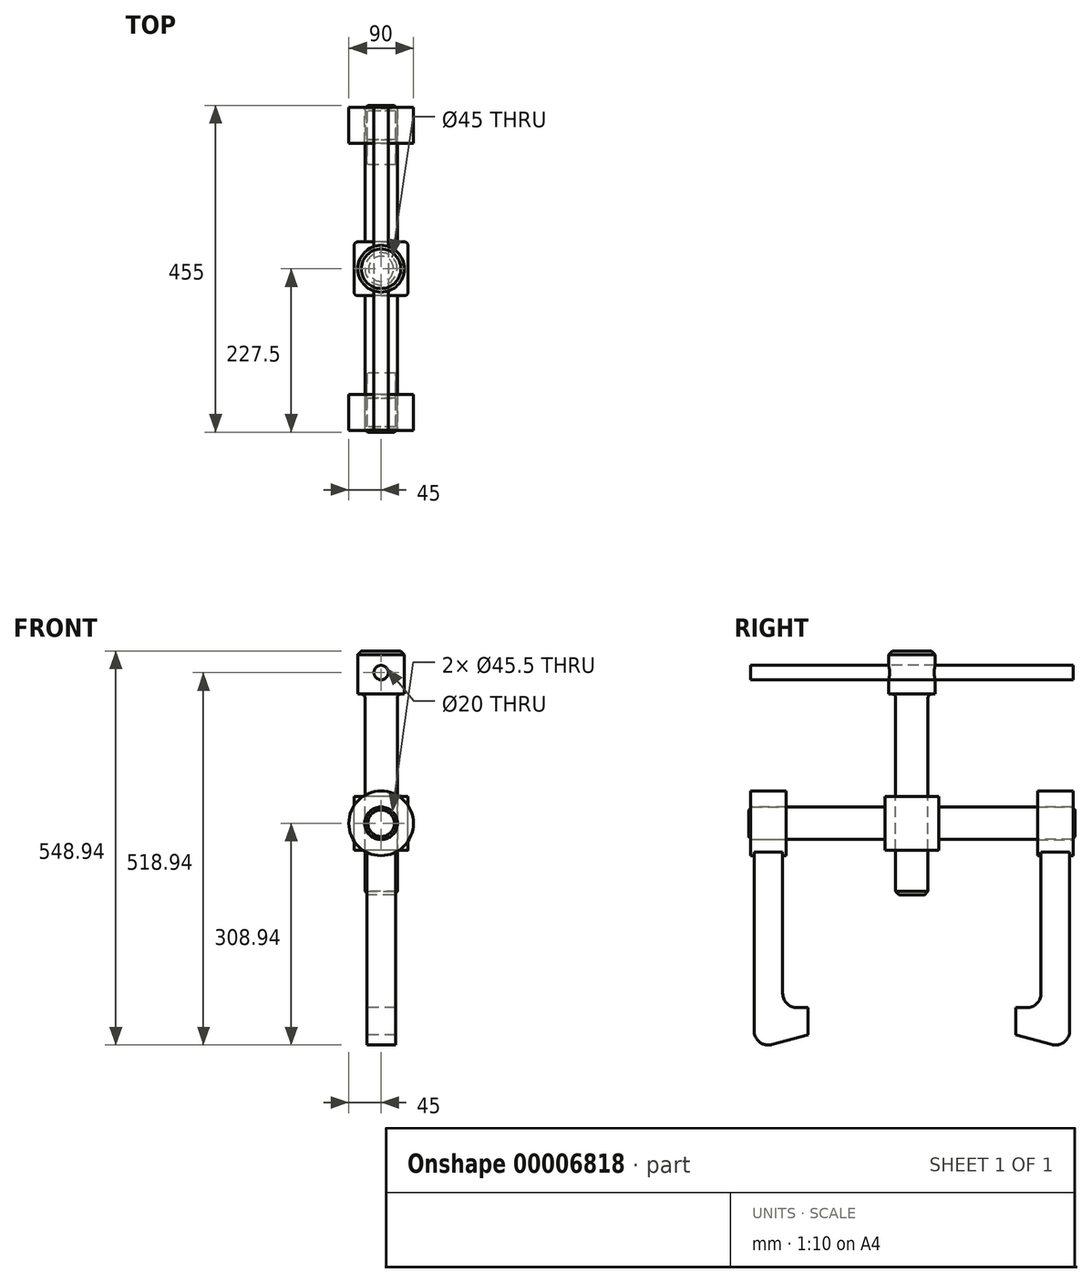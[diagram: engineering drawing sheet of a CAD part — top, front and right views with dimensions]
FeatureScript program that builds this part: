
annotation { "Feature Type Name" : "Feature", "Feature Type Description" : "" }
export const myFeature = defineFeature(function(context is Context, id is Id, definition is map)
    precondition{}
    {
        {
            var Q0;
            Q0=qCreatedBy(makeId("Right.planeOp"),FACE);
            var sketch = newSketch(context, id + "F0", { "sketchPlane" : qUnion([Q0])});
            skLineSegment(sketch, "E0.rect.bottom", {"start": v(-37.5, -37.5) * mm, "end": v(37.5, -37.5) * mm});
            skLineSegment(sketch, "E0.rect.top", {"start": v(-37.5, 37.5) * mm, "end": v(37.5, 37.5) * mm});
            skLineSegment(sketch, "E0.rect.left", {"start": v(-37.5, -37.5) * mm, "end": v(-37.5, 37.5) * mm});
            skLineSegment(sketch, "E0.rect.right", {"start": v(37.5, -37.5) * mm, "end": v(37.5, 37.5) * mm});
            skPoint(sketch, "E0.rect.middle", {"position": v(0, 0) * mm});
            skSolve(sketch);
        }
        {
            var Q0;
            Q0 = qSketchRegion(id + "F0", true);
            extrude(context, id + "F1", {"entities" : qUnion([Q0]), "endBound" : BoundingType.SYMMETRIC, "depth" : 75 * mm});
        }
        {
            var Q0;
            Q0=makeQuery(id+"F1.opExtrude","CAP_EDGE",EDGE,{"disambiguationData":[OSD([sQuery(id+"F0.wireOp",EDGE,"E0.rect.left")])],"isStart":false});
            var Q1;
            Q1=makeQuery(id+"F1.opExtrude","CAP_EDGE",EDGE,{"disambiguationData":[OSD([sQuery(id+"F0.wireOp",EDGE,"E0.rect.right")])],"isStart":false});
            var Q2;
            Q2=makeQuery(id+"F1.opExtrude","CAP_EDGE",EDGE,{"disambiguationData":[OSD([sQuery(id+"F0.wireOp",EDGE,"E0.rect.left")])],"isStart":true});
            var Q3;
            Q3=makeQuery(id+"F1.opExtrude","CAP_EDGE",EDGE,{"disambiguationData":[OSD([sQuery(id+"F0.wireOp",EDGE,"E0.rect.right")])],"isStart":true});
            fillet(context, id + "F2", {"entities" : qUnion([Q0, Q1, Q2, Q3]), "radius" : 5 * mm, "tangentPropagation" : true, "allowEdgeOverflow" : false});
        }
        {
            var Q0;
            Q0=makeQuery(id+"F1.opExtrude","SWEPT_FACE",FACE,{"disambiguationData":[OSD([sQuery(id+"F0.wireOp",EDGE,"E0.rect.top")])]});
            var sketch = newSketch(context, id + "F3", { "sketchPlane" : qUnion([Q0])});
            skCircle(sketch, "E1", {"center": v(0, 0) * mm, "radius": 22.5 * mm});
            skSolve(sketch);
        }
        {
            var Q0;
            Q0 = qSketchRegion(id + "F3", true);
            extrude(context, id + "F4", {"entities" : qUnion([Q0]), "operationType" : NewBodyOperationType.REMOVE, "endBound" : BoundingType.THROUGH_ALL, "oppositeDirection" : true, "depth" : 25 * mm});
        }
        {
            var Q0;
            Q0=makeQuery(id+"F1.opExtrude","SWEPT_FACE",FACE,{"disambiguationData":[OSD([sQuery(id+"F0.wireOp",EDGE,"E0.rect.left")])]});
            var sketch = newSketch(context, id + "F5", { "sketchPlane" : qUnion([Q0])});
            skCircle(sketch, "E2", {"center": v(0, 0) * mm, "radius": 22.5 * mm});
            skSolve(sketch);
        }
        {
            var Q0;
            Q0 = qSketchRegion(id + "F5", true);
            extrude(context, id + "F6", {"entities" : qUnion([Q0]), "depth" : 190 * mm});
        }
        {
            var Q0;
            Q0=makeQuery(id+"F6.opExtrude","SWEPT_BODY",BODY,{"disambiguationData":[OSD([sQuery(id+"F5.wireOp",EDGE,"E2")])]});
            var Q1;
            Q1=qCreatedBy(makeId("Front.planeOp"),FACE);
            mirror(context, id + "F7", {"entities" : qUnion([Q0]), "mirrorPlane" : qUnion([Q1])});
        }
        {
            var Q0;
            Q0=makeQuery(id+"F6.opExtrude","CAP_EDGE",EDGE,{"disambiguationData":[OSD([sQuery(id+"F5.wireOp",EDGE,"E2")])],"isStart":false});
            var Q1;
            Q1=makeQuery(id+"F7.opPattern","COPY",EDGE,{"derivedFrom":makeQuery(id+"F6.opExtrude","CAP_EDGE",EDGE,{"disambiguationData":[OSD([sQuery(id+"F5.wireOp",EDGE,"E2")])],"isStart":false}),"instanceName":"1"});
            chamfer(context, id + "F8", {"entities" : qUnion([Q0, Q1]), "width" : 4 * mm, "tangentPropagation" : true});
        }
        {
            var Q0;
            Q0=qCreatedBy(makeId("Front.planeOp"),FACE);
            var sketch = newSketch(context, id + "F9", { "sketchPlane" : qUnion([Q0])});
            skLineSegment(sketch, "E3", {"start": v(0, -100) * mm, "end": v(0, 240) * mm});
            skLineSegment(sketch, "E4", {"start": v(0, 240) * mm, "end": v(32.5, 240) * mm});
            skLineSegment(sketch, "E5", {"start": v(32.5, 240) * mm, "end": v(32.5, 180) * mm});
            skLineSegment(sketch, "E6", {"start": v(32.5, 180) * mm, "end": v(22.5, 180) * mm});
            skLineSegment(sketch, "E7", {"start": v(22.5, 180) * mm, "end": v(22.5, -100) * mm});
            skLineSegment(sketch, "E8", {"start": v(22.5, -100) * mm, "end": v(0, -100) * mm});
            skSolve(sketch);
        }
        {
            var Q0;
            Q0 = qSketchRegion(id + "F9", true);
            var Q1;
            Q1=sQuery(id+"F9.wireOp",EDGE,"E3");
            revolve(context, id + "F10", {"entities" : qUnion([Q0]), "axis" : qUnion([Q1]), "revolveType" : RevolveType.FULL});
        }
        {
            var Q0;
            Q0=makeQuery(id+"F10.opRevolve","SWEPT_EDGE",EDGE,{"disambiguationData":[OSD([sQuery(id+"F9.wireOp",EDGE,"E4"),sQuery(id+"F9.wireOp",EDGE,"E5")])]});
            var Q1;
            Q1=makeQuery(id+"F10.opRevolve","SWEPT_EDGE",EDGE,{"disambiguationData":[OSD([sQuery(id+"F9.wireOp",EDGE,"E7"),sQuery(id+"F9.wireOp",EDGE,"E8")])]});
            chamfer(context, id + "F11", {"entities" : qUnion([Q0, Q1]), "width" : 5 * mm, "tangentPropagation" : true});
        }
        {
            var Q0;
            Q0=makeQuery(id+"F10.opRevolve","SWEPT_EDGE",EDGE,{"disambiguationData":[OSD([sQuery(id+"F9.wireOp",EDGE,"E6"),sQuery(id+"F9.wireOp",EDGE,"E7")])]});
            fillet(context, id + "F12", {"entities" : qUnion([Q0]), "radius" : 5 * mm, "tangentPropagation" : true, "allowEdgeOverflow" : false});
        }
        {
            var Q0;
            Q0=qCreatedBy(makeId("Front.planeOp"),FACE);
            cPlane(context, id + "F13", {"entities" : qUnion([Q0]), "cplaneType" : CPlaneType.OFFSET, "offset" : 200 * mm, "width" : 150 * mm, "height" : 150 * mm});
        }
        {
            var Q0;
            Q0=qCreatedBy(id+"F13.planeOp",FACE);
            var sketch = newSketch(context, id + "F14", { "sketchPlane" : qUnion([Q0])});
            skCircle(sketch, "E9", {"center": v(0, 0) * mm, "radius": 22.75 * mm});
            skCircle(sketch, "E10", {"center": v(0, 0) * mm, "radius": 45 * mm});
            skSolve(sketch);
        }
        {
            var Q0;
            Q0 = qSketchRegion(id + "F14", true);
            extrude(context, id + "F15", {"entities" : qUnion([Q0]), "endBound" : BoundingType.SYMMETRIC, "oppositeDirection" : true, "depth" : 50 * mm});
        }
        {
            var Q0;
            Q0=qCreatedBy(makeId("Right.planeOp"),FACE);
            var sketch = newSketch(context, id + "F16", { "sketchPlane" : qUnion([Q0])});
            skLineSegment(sketch, "E11", {"start": v(-220, -35) * mm, "end": v(-220, -288.94) * mm});
            skLineSegment(sketch, "E12", {"start": v(-194.82, -308.25) * mm, "end": v(-145, -294.9) * mm});
            skLineSegment(sketch, "E13", {"start": v(-145, -294.9) * mm, "end": v(-145, -256.9) * mm});
            skLineSegment(sketch, "E14", {"start": v(-145, -256.9) * mm, "end": v(-160, -256.9) * mm});
            skLineSegment(sketch, "E15", {"start": v(-180, -236.9) * mm, "end": v(-180, -35) * mm});
            skLineSegment(sketch, "E16", {"start": v(-180, -35) * mm, "end": v(-220, -35) * mm});
            skLineSegment(sketch, "E17", {"start": v(-220, -315) * mm, "end": v(-172.36, -315) * mm, "construction": true});
            skPoint(sketch, "E18.visualSharp", {"position": v(-220, -315) * mm});
            skArc(sketch, "E18.filletArc", {"start": v(-220, -288.94) * mm, "mid": v(-212.18, -304.8) * mm, "end": v(-194.82, -308.25) * mm});
            skPoint(sketch, "E19.visualSharp", {"position": v(-180, -256.9) * mm});
            skArc(sketch, "E19.filletArc", {"start": v(-180, -236.9) * mm, "mid": v(-174.14, -251.05) * mm, "end": v(-160, -256.9) * mm});
            skSolve(sketch);
        }
        {
            var Q0;
            Q0 = qSketchRegion(id + "F16", true);
            extrude(context, id + "F17", {"entities" : qUnion([Q0]), "operationType" : NewBodyOperationType.ADD, "endBound" : BoundingType.SYMMETRIC, "depth" : 40 * mm});
        }
        {
            var Q0;
            Q0=makeQuery(id+"F15.opExtrude","SWEPT_BODY",BODY,{"disambiguationData":[OSD([sQuery(id+"F14.wireOp",EDGE,"E9"),sQuery(id+"F14.wireOp",EDGE,"E10")])]});
            var Q1;
            Q1=qCreatedBy(makeId("Front.planeOp"),FACE);
            mirror(context, id + "F18", {"entities" : qUnion([Q0]), "mirrorPlane" : qUnion([Q1])});
        }
        {
            var Q0;
            Q0=qCreatedBy(makeId("Front.planeOp"),FACE);
            var sketch = newSketch(context, id + "F19", { "sketchPlane" : qUnion([Q0])});
            skCircle(sketch, "E20", {"center": v(0, 210) * mm, "radius": 10 * mm});
            skSolve(sketch);
        }
        {
            var Q0;
            Q0 = qSketchRegion(id + "F19", true);
            var Q1;
            Q1=makeQuery(id+"F10.opRevolve","SWEPT_FACE",FACE,{"disambiguationData":[OSD([sQuery(id+"F9.wireOp",EDGE,"E5")])]});
            extrude(context, id + "F20", {"entities" : qUnion([Q0]), "operationType" : NewBodyOperationType.REMOVE, "endBound" : BoundingType.UP_TO_SURFACE, "oppositeDirection" : true, "endBoundEntityFace" : qUnion([Q1]), "depth" : 25 * mm});
        }
        {
            var Q0;
            Q0=makeQuery(id+"F20.boolean.opBoolean","COPY",FACE,{"derivedFrom":makeQuery(id+"F20.opExtrude","CAP_FACE",FACE,{"disambiguationData":[OSD([sQuery(id+"F19.wireOp",EDGE,"E20")])],"isStart":true})});
            var sketch = newSketch(context, id + "F21", { "sketchPlane" : qUnion([Q0])});
            skCircle(sketch, "E21.0", {"center": v(0, 210) * mm, "radius": 10 * mm});
            skSolve(sketch);
        }
        {
            var Q0;
            Q0 = qSketchRegion(id + "F21", true);
            var Q1;
            Q1=makeQuery(id+"F10.opRevolve","SWEPT_FACE",FACE,{"disambiguationData":[OSD([sQuery(id+"F9.wireOp",EDGE,"E5")])]});
            extrude(context, id + "F22", {"entities" : qUnion([Q0]), "operationType" : NewBodyOperationType.REMOVE, "endBound" : BoundingType.UP_TO_SURFACE, "oppositeDirection" : true, "endBoundEntityFace" : qUnion([Q1]), "depth" : 25 * mm});
        }
        {
            var Q0;
            Q0=qCreatedBy(makeId("Front.planeOp"),FACE);
            var sketch = newSketch(context, id + "F23", { "sketchPlane" : qUnion([Q0])});
            skCircle(sketch, "E22.0", {"center": v(0, 210) * mm, "radius": 10 * mm});
            skSolve(sketch);
        }
        {
            var Q0;
            Q0 = qSketchRegion(id + "F23", true);
            extrude(context, id + "F24", {"entities" : qUnion([Q0]), "endBound" : BoundingType.SYMMETRIC, "depth" : 450 * mm});
        }
    });
